# Revit family: Reece_Basin_American Standard_Acacia SupaSleek_Vessel Basin_550 mm
name_source: partatom
category: Plumbing Fixtures
revit_build: Autodesk Revit 2018 (Build: 20180329_1100(x64)
units: mm (PartAtom-declared; Revit-internal decimal feet)

## family parameters
Cut with Voids When Loaded = No
Host = Face
Part Type = Normal
Room Calculation Point = Yes
Round Connector Dimension = Use Diameter
Shared = Yes

## types (1)
- No Taphole_Fine Fire Clay Ceramic
    CWFU = 0
    Default Elevation = 1000 mm
    Description = American Standard Acacia SupaSleek Vessel Basin 550mm No Tap Hole White
    Disclaimer = THIS FILE IS THE PROPERTY OF THE REECE GROUP. IT MAY NOT BE REPRODUCED, REVERSE-ENGINEERED OR MODIFIED. ANY REPUBLICATION, TRANSMISSION OR DISTRIBUTION FOR THE PURPOSE OF COMMERCIALLY EXPLOITING THE FILES IS PROHIBITED.
    HWFU = 0
    Keynote = Product #9509618, Reece_Basin_American Standard_Acacia SupaSleek_Vessel Basin_550 mm - No Taphole_Fine Fire Clay Ceramic
    Manufacturer = American Standard
    Model = Acacia SupaSleek
    Reece_Basin_Outlet = 32 mm
    Reece_Detail_Additional = No Overflow
    Reece_Detail_Connector = No Taphole
    Reece_Detail_Disclaimer = THIS FILE IS THE PROPERTY OF THE REECE GROUP. IT MAY NOT BE REPRODUCED, REVERSE-ENGINEERED OR MODIFIED. ANY REPUBLICATION, TRANSMISSION OR DISTRIBUTION FOR THE PURPOSE OF COMMERCIALLY EXPLOITING THE FILES IS PROHIBITED.
    Reece_Detail_Installation = Vessel Basin
    Reece_Material_Main = Reece_Ceramic_Fine Fire Clay_White
    Reece_Overall_Capacity = 5 L
    Reece_Overall_Depth = 380 mm
    Reece_Overall_Height = 110 mm
    Reece_Overall_Width = 550 mm
    Reece_Product_Brand = American Standard
    Reece_Product_Description = American Standard Acacia SupaSleek Vessel Basin 550mm No Taphole White
    Reece_Product_Mount = Above Counter
    Reece_Product_Number = 9509618
    Reece_Product_Sub Brand = Acacia SupaSleek
    Reece_Product_Type = Basin
    Reece_Product_Web Page = https://www.reece.com.au
    Type Comments = Basin
    URL = https://www.reece.com.au
    WFU = 0

## geometry (parser evidence)
native form markers: Sweep x2
no freeform markers — native parametric forms only
